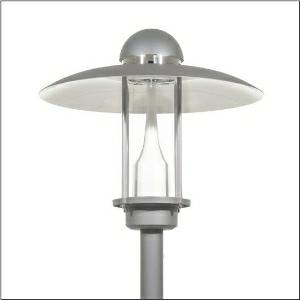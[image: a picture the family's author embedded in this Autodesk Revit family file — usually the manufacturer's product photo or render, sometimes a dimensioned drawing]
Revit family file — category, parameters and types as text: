
# Revit family: city-light_elegance_iq___p1_0a_5xa5265lf14hp_2e01
name_source: partatom
category: Lighting Fixtures
units: mm (PartAtom-declared; Revit-internal decimal feet)

## family parameters
Cut with Voids When Loaded = No
Host = Face
Light Source = No
Part Type = Normal
Room Calculation Point = No
Round Connector Dimension = Use Diameter
Shared = No

## types (1)
- --- (1 x LED, 4690 lm, 33.6 W, 4000K)
    Apparent Load = 34 VA
    CIE Flux Codes = 31 62 91 97 100
    Color Rendering = 70
    Color Temperature = 4000K
    Default Elevation = 1800 mm
    Description = City-Light Elegance iQ, mast luminaire, Module 540 iQ-SR, primary light control with 3 zone facetted reflector, of plastic, silver coated, highly specular, structured, primary optical cover: cover, of PMMA, transparent, light distribution: P1.0a, light emission: direct distribution, primary light characteristic: strongly asymmetric, installation type: post-top, LED, High Power LED, rated luminous flux: 4.690lm, luminous efficacy: 140lm/W, light colour: 740, colour temperature: 4000K, control gear: iQ Street-Remote, control: pre-setting: logarithmic dimming characteristic, Street-Remote, Auto-Match, Temp-Guard, Lumen-Switch, Night-Set, Smart-Wire, Light-Fading, Desk-Remote (wireless, voltage-free reading and setting of iQ features in the workshop via application-optimized NFC function/RFID function), optimised constant luminous flux control (CLO 2.0), with terminal, 6-pole, max. 2.5mm², mains connection: 230..240V, AC, 50/60Hz, start of lifetime: 34W, end of service life: 36W, reduction: 15W, luminaire housing, upper part, of aluminium, coated, Siteco® metallic grey (DB 702S), diameter: 750mm, height: 675mm, spigot size: d x l = 76 x 70mm (post-top) | with reducer (optional accessory) 60 x 70mm, mounting height: 3..5m, post-top mast mounting element, of diecast aluminium, coated, Siteco® metallic grey (DB 702S), Module 540 iQ-SR, traffic white (RAL 9016), equipment: standard, protection rating (complete): IP65, insulation class (complete): insulation class II (safety insulation), certification: CE, ENEC, VDE, packaging unit: 1 piece

Light Distribution: P1.0a
    Height = 675 mm
    Lamp = 1 x LED
    Lamp Light Flux = 4690 lm
    Lamp Power = 33.6 W
    Lamp count = 1
    Length = 750 mm
    Luminous efficacy = 140 lm/W
    Manufacturer = Siteco
    ModVariant = No
    Model = 5XA5265LF14HP
    Number of Poles = 1
    OnlyDefault = Yes
    Power Factor = 1
    Product Name = City-Light Elegance iQ | P1.0a
    Product group = mast luminaire | pylon top
    ProductGroupID = 6100
    Protection Class = Protection class II
    Protection Degree = IP 65
    RLX_Detail_Level = 1
    RLX_Emergency_Light_Flux = 0 lm
    RLX_Emergency_Type = 0
    RLX_Emergency_Type_DB = No
    RlxData = <blob elided: 36853 chars, md5=9d0e9126>
    Socket = socket
    Standby Power = 0 W
    System Light Flux = 4690 lm
    System Power = 34 W
    Type Comments = factory setting: luminous flux: 100 % | dim-lin: 254 | 695 mA
    Type Image = l_1006912.jpg
    URL = http://relux.com
    VarID = @adj_192936
    Voltage = 0 V
    Weight = 0.00 kg
    Width = 0 mm  [stored 0 ft]

note: [stored X ft] marks values corroborated as IEEE doubles in the binary element streams (Revit-internal decimal feet)

## geometry (parser evidence)
native form markers: Blend x4, Sweep x11
no freeform markers — native parametric forms only
